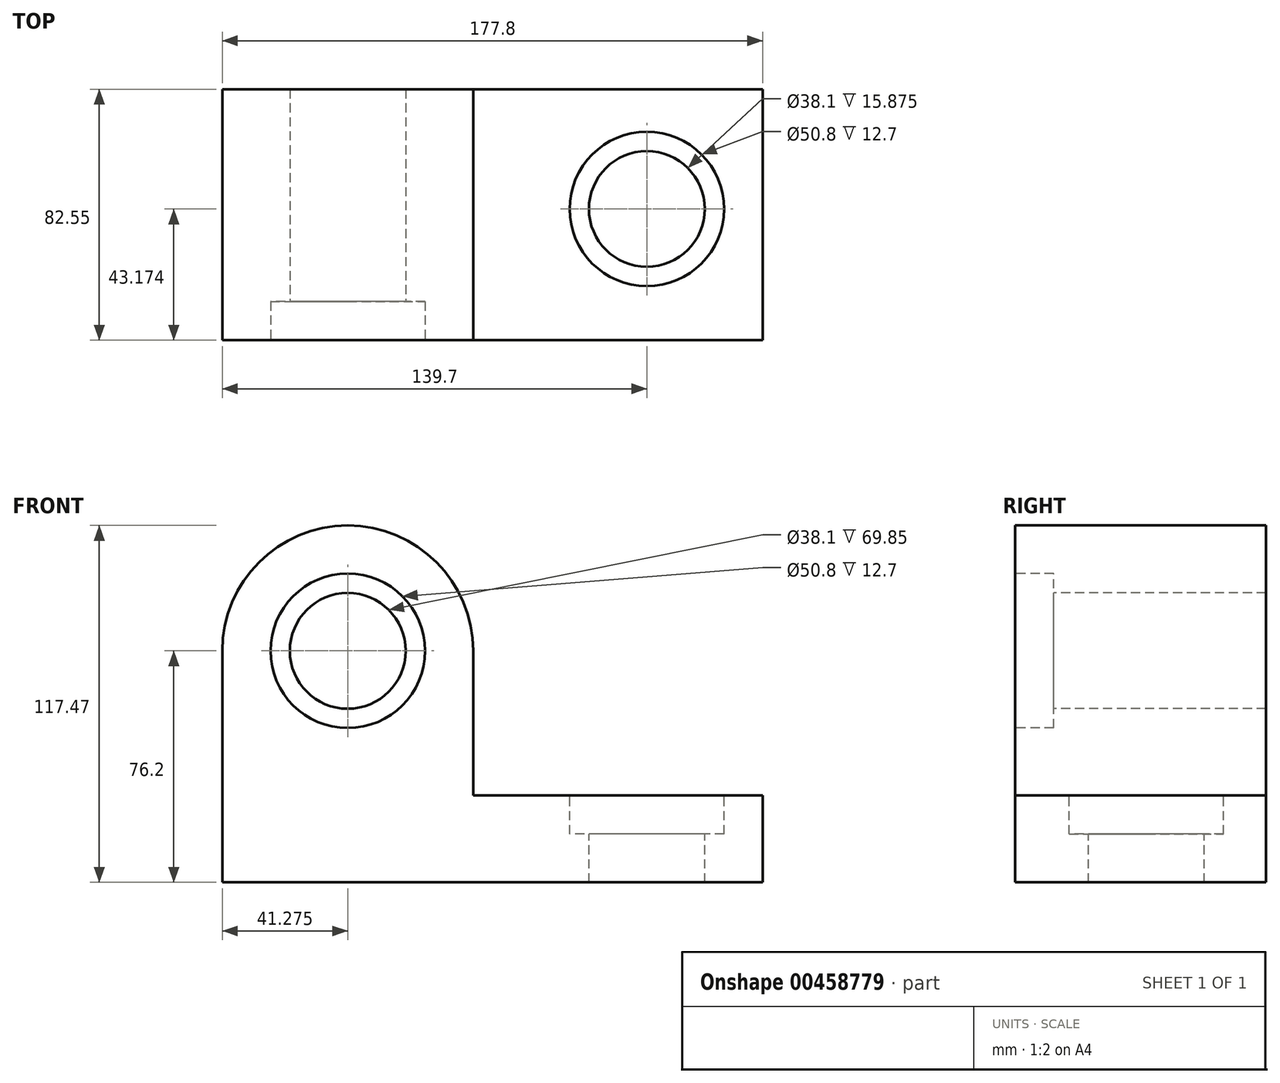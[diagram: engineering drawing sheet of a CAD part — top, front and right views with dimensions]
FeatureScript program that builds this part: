
annotation { "Feature Type Name" : "Feature", "Feature Type Description" : "" }
export const myFeature = defineFeature(function(context is Context, id is Id, definition is map)
    precondition{}
    {
        {
            var Q0;
            Q0=qCreatedBy(makeId("Front.planeOp"),FACE);
            var sketch = newSketch(context, id + "F0", { "sketchPlane" : qUnion([Q0])});
            skLineSegment(sketch, "E0", {"start": v(0, 0) * mm, "end": v(177.8, 0) * mm});
            skLineSegment(sketch, "E1", {"start": v(177.8, 0) * mm, "end": v(177.8, 28.57) * mm});
            skLineSegment(sketch, "E2", {"start": v(177.8, 28.58) * mm, "end": v(82.55, 28.57) * mm});
            skLineSegment(sketch, "E3", {"start": v(0, 0) * mm, "end": v(0, 76.2) * mm});
            skLineSegment(sketch, "E4", {"start": v(82.55, 28.57) * mm, "end": v(82.55, 76.2) * mm});
            skArc(sketch, "E5", {"start": v(82.55, 76.2) * mm, "mid": v(41.28, 117.48) * mm, "end": v(0, 76.2) * mm});
            skArc(sketch, "E6", {"start": v(0, 76.2) * mm, "mid": v(41.28, 117.48) * mm, "end": v(82.55, 76.2) * mm});
            skSolve(sketch);
        }
        {
            var Q0;
            Q0=makeQuery(id+"F0.imprint","IMPRINT",FACE,{"disambiguationData":[TD([[makeQuery(id+"F0.imprint","IMPRINT",EDGE,{"derivedFrom":sQuery(id+"F0.wireOp",EDGE,"E0")}),1.0]])]});
            extrude(context, id + "F1", {"entities" : qUnion([Q0]), "depth" : 82.55 * mm});
        }
        {
            var Q0;
            Q0=makeQuery(id+"F1.opExtrude","CAP_FACE",FACE,{"disambiguationData":[OSD([sQuery(id+"F0.wireOp",EDGE,"E0"),sQuery(id+"F0.wireOp",EDGE,"E1"),sQuery(id+"F0.wireOp",EDGE,"E2"),sQuery(id+"F0.wireOp",EDGE,"E3"),sQuery(id+"F0.wireOp",EDGE,"E4"),sQuery(id+"F0.wireOp",EDGE,"E6")])],"isStart":false});
            var sketch = newSketch(context, id + "F2", { "sketchPlane" : qUnion([Q0])});
            skPoint(sketch, "E7", {"position": v(41.28, 76.2) * mm});
            skSolve(sketch);
        }
        {
            var Q0;
            Q0=makeQuery(id+"F1.opExtrude","SWEPT_FACE",FACE,{"disambiguationData":[OSD([sQuery(id+"F0.wireOp",EDGE,"E2")])]});
            var sketch = newSketch(context, id + "F3", { "sketchPlane" : qUnion([Q0])});
            skPoint(sketch, "E8", {"position": v(139.7, -39.38) * mm});
            skSolve(sketch);
        }
        {
            var Q0;
            Q0=sQuery(id+"F2.wireOp",VERTEX,"E7");
            var Q1;
            Q1=makeQuery(id+"F1.opExtrude","SWEPT_BODY",BODY,{"disambiguationData":[OSD([sQuery(id+"F0.wireOp",EDGE,"E0"),sQuery(id+"F0.wireOp",EDGE,"E1"),sQuery(id+"F0.wireOp",EDGE,"E2"),sQuery(id+"F0.wireOp",EDGE,"E3"),sQuery(id+"F0.wireOp",EDGE,"E4"),sQuery(id+"F0.wireOp",EDGE,"E6")])]});
            hole(context, id + "F4", {"style" : HoleStyle.C_BORE, "endStyle" : HoleEndStyle.THROUGH, "holeDiameter" : 38.1 * mm, "cBoreDiameter" : 50.8 * mm, "cBoreDepth" : 12.7 * mm, "isTappedThrough" : true, "tappedDepth" : 12.7 * mm, "tapClearance" : 3, "locations" : qUnion([Q0]), "scope" : qUnion([Q1])});
        }
        {
            var Q0;
            Q0=sQuery(id+"F3.wireOp",VERTEX,"E8");
            var Q1;
            Q1=makeQuery(id+"F1.opExtrude","SWEPT_BODY",BODY,{"disambiguationData":[OSD([sQuery(id+"F0.wireOp",EDGE,"E0"),sQuery(id+"F0.wireOp",EDGE,"E1"),sQuery(id+"F0.wireOp",EDGE,"E2"),sQuery(id+"F0.wireOp",EDGE,"E3"),sQuery(id+"F0.wireOp",EDGE,"E4"),sQuery(id+"F0.wireOp",EDGE,"E6")])]});
            hole(context, id + "F5", {"style" : HoleStyle.C_BORE, "endStyle" : HoleEndStyle.THROUGH, "holeDiameter" : 38.1 * mm, "cBoreDiameter" : 50.8 * mm, "cBoreDepth" : 12.7 * mm, "isTappedThrough" : true, "tappedDepth" : 12.7 * mm, "tapClearance" : 3, "locations" : qUnion([Q0]), "scope" : qUnion([Q1])});
        }
    });
